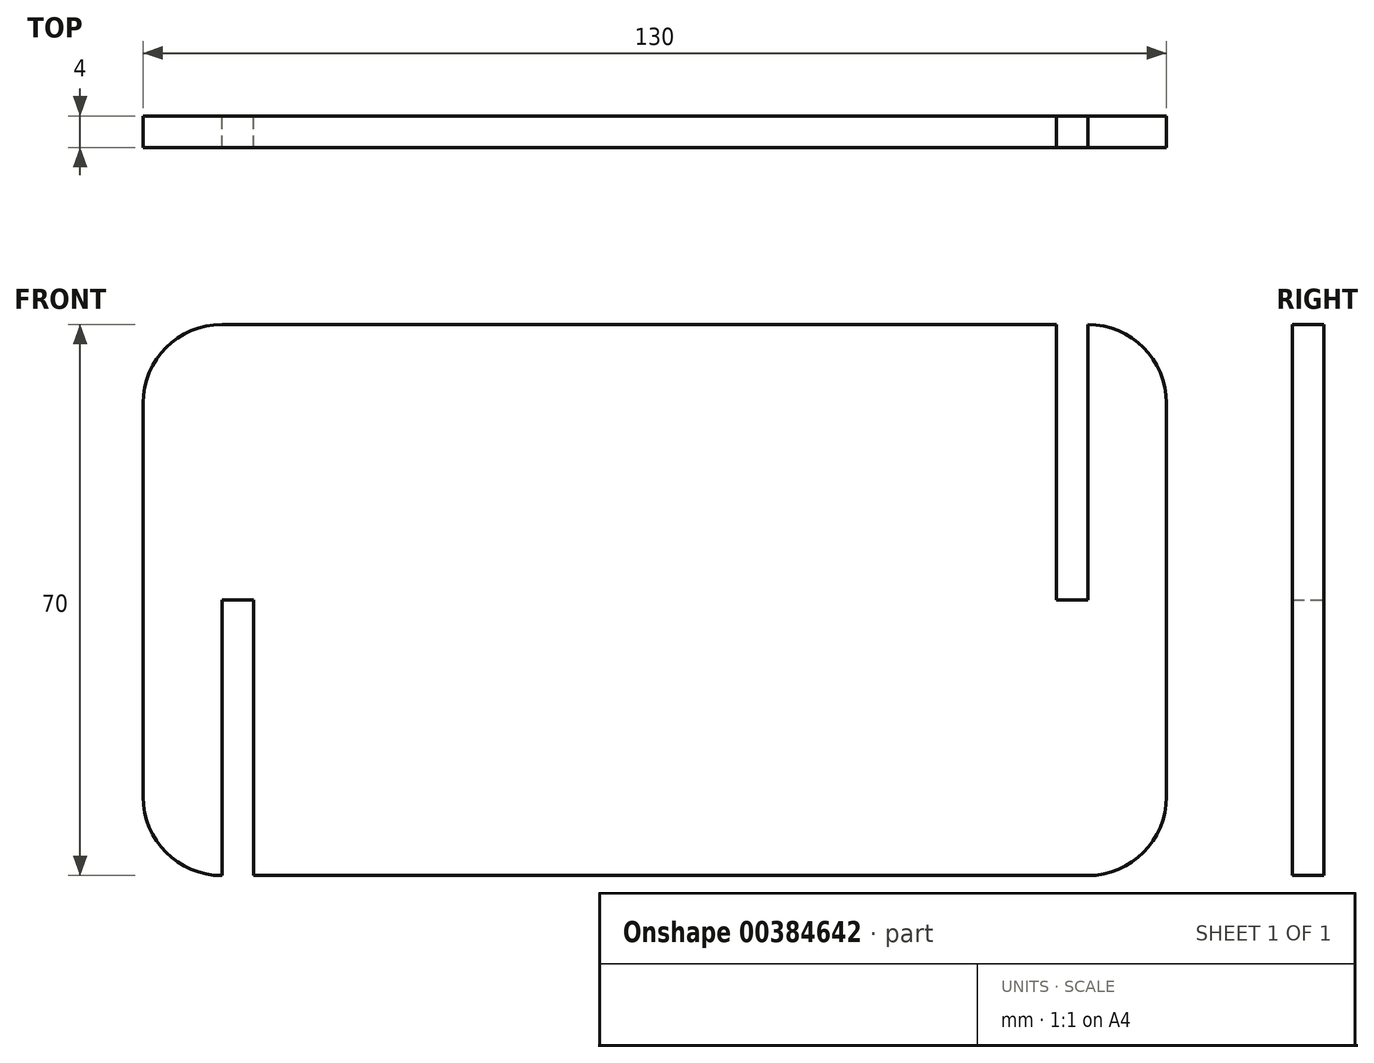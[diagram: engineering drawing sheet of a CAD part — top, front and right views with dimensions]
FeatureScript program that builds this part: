
annotation { "Feature Type Name" : "Feature", "Feature Type Description" : "" }
export const myFeature = defineFeature(function(context is Context, id is Id, definition is map)
    precondition{}
    {
        {
            var Q0;
            Q0=qCreatedBy(makeId("Front.planeOp"),FACE);
            var sketch = newSketch(context, id + "F0", { "sketchPlane" : qUnion([Q0])});
            skLineSegment(sketch, "E0.bottom", {"start": v(-55, 35) * mm, "end": v(51, 35) * mm});
            skLineSegment(sketch, "E0.top", {"start": v(-51, -35) * mm, "end": v(55, -35) * mm});
            skLineSegment(sketch, "E0.left", {"start": v(-65, 25) * mm, "end": v(-65, -25) * mm});
            skLineSegment(sketch, "E0.right", {"start": v(65, 25) * mm, "end": v(65, -25) * mm});
            skPoint(sketch, "E1.visualSharp", {"position": v(-65, 35) * mm});
            skArc(sketch, "E1.filletArc", {"start": v(-55, 35) * mm, "mid": v(-62.07, 32.07) * mm, "end": v(-65, 25) * mm});
            skPoint(sketch, "E2.visualSharp", {"position": v(-65, -35) * mm});
            skArc(sketch, "E2.filletArc", {"start": v(-65, -25) * mm, "mid": v(-62.07, -32.07) * mm, "end": v(-55, -35) * mm});
            skPoint(sketch, "E3.visualSharp", {"position": v(65, -35) * mm});
            skArc(sketch, "E3.filletArc", {"start": v(55, -35) * mm, "mid": v(62.07, -32.07) * mm, "end": v(65, -25) * mm});
            skPoint(sketch, "E4.visualSharp", {"position": v(65, 35) * mm});
            skArc(sketch, "E4.filletArc", {"start": v(65, 25) * mm, "mid": v(62.07, 32.07) * mm, "end": v(55, 35) * mm});
            skLineSegment(sketch, "E5.top", {"start": v(-55, 0) * mm, "end": v(-51, 0) * mm});
            skLineSegment(sketch, "E5.left", {"start": v(-55, -35) * mm, "end": v(-55, 0) * mm});
            skLineSegment(sketch, "E5.right", {"start": v(-51, -35) * mm, "end": v(-51, 0) * mm});
            skLineSegment(sketch, "E6.top", {"start": v(55, 0) * mm, "end": v(51, 0) * mm});
            skLineSegment(sketch, "E6.left", {"start": v(55, 35) * mm, "end": v(55, 0) * mm});
            skLineSegment(sketch, "E6.right", {"start": v(51, 35) * mm, "end": v(51, 0) * mm});
            skSolve(sketch);
        }
        {
            var Q0;
            Q0=qSketchRegion(id+"F0",true);
            extrude(context, id + "F1", {"entities" : qUnion([Q0]), "depth" : 4 * mm});
        }
    });
